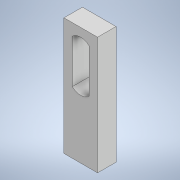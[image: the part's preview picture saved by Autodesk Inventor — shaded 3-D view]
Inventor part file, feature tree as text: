
AUTODESK INVENTOR PART (.ipt)
format: ipt  version: 2022 (Build 260153000, 153)  size: 116,736 bytes
history: native  units: mm
features: other x1, extrude x1, sketch x1
ambient origin geometry x8: Origin, YZ Plane, XZ Plane, XY Plane, X Axis, Y Axis, Z Axis, Center Point
bodies: Body1 (feature_tree)
feature tree (3):
  other  "Sólido1"
  extrude  "Extrusión1"  Depth=5.5mm TaperAngle=0.0deg
  sketch  "Boceto1"  dims[d0=5.0mm d1=25.0mm d2=30.0mm d3=10.0mm d4=20.0mm d5=5.0mm d6=15.0mm d7=1.0mm d8=5.5mm d9=0.0mm]
